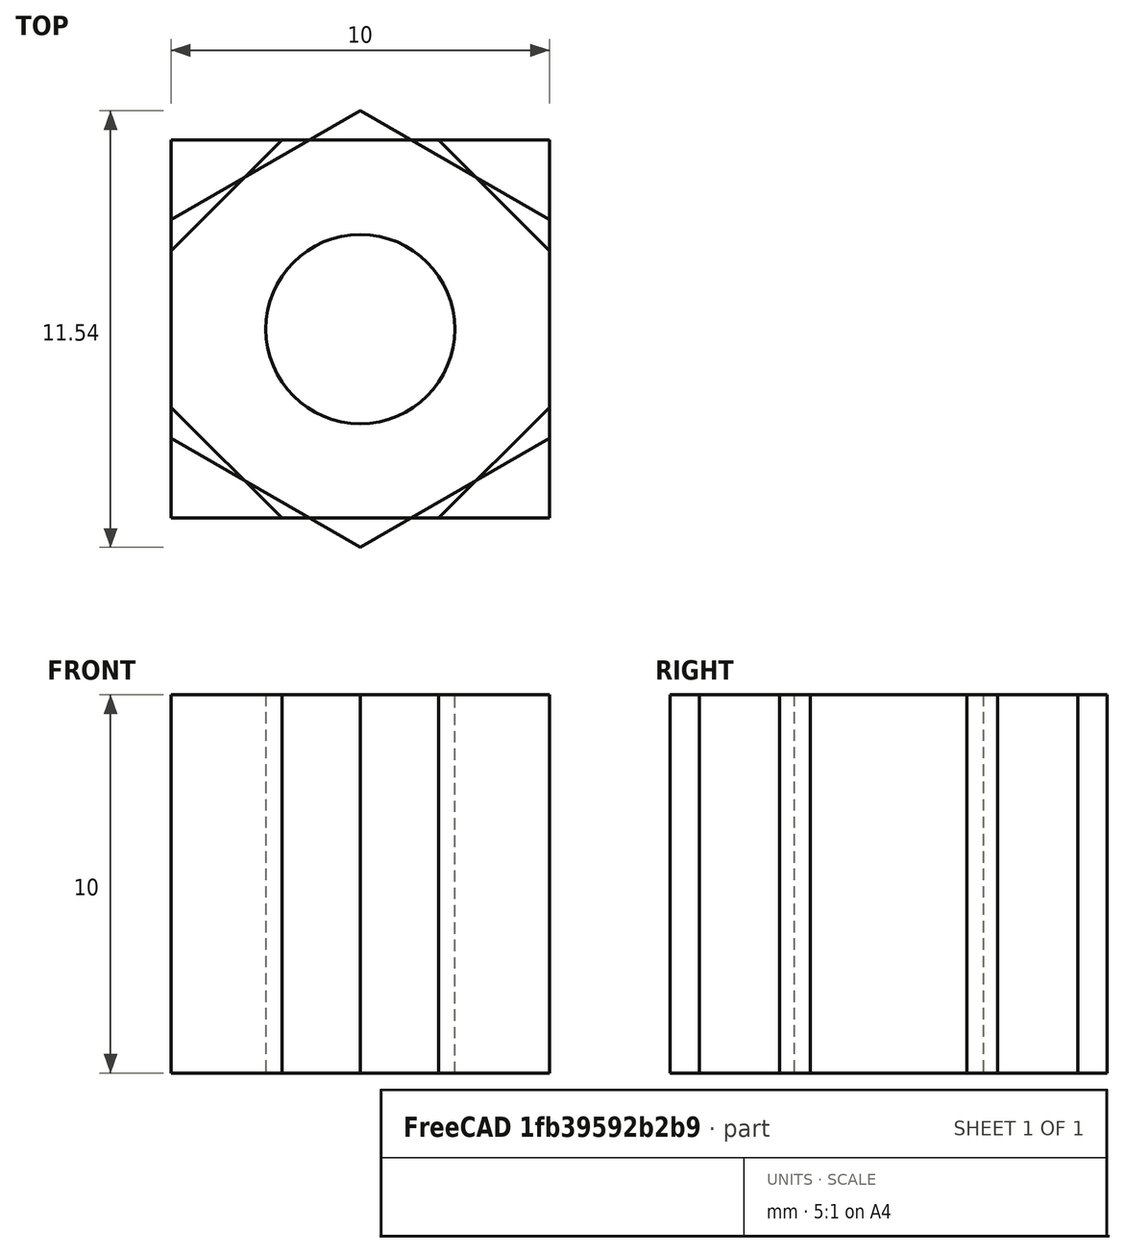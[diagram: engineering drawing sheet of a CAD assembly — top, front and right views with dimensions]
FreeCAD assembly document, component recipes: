
FREECAD ASSEMBLY — COMPONENT RECIPES ("xchg-components-b")

This assembly document has 6 components, labeled P0..P5 below (a component is one placed body or linked part). 6 of them carry a construction recipe — the FreeCAD feature program that regenerates the part from scratch, quoted from this document or its linked companion documents; the rest are supplied as boundary geometry only. No exploded tour is included for this assembly.
COMPONENT P0 — recipe-attached ("Cylinder 001", modeled in this document).
Construction recipe (the document's own serialized feature program — sketch geometry with constraints, then the solid features built on it; lengths are millimeters unless a unit is written):

FEATURE [Sketcher::SketchObject] Sketch
  MapMode = 5
  Support = -> [XY_Plane]
  sketch-geometry (1):
    g0: Circle CenterX=0 CenterY=0 CenterZ=0 NormalX=0 NormalY=0 NormalZ=1 AngleXU=0 Radius=2.5
  constraints (2):
    c: Coincident(g0,g-1)
    c: Diameter(g0) = 5
FEATURE [PartDesign::Pad] Pad
  ClaimChildren = false
  Length = 10
  Length2 = 100
  Profile = -> Sketch
  Type = 0
FEATURE [PartDesign::Body] Body  label="Cylinder 000"
  Group = -> [Sketch,Pad]
  Origin = -> Origin
  Tip = -> Pad
COMPONENT P1 — recipe-attached ("Cube 001", modeled in this document).
Construction recipe (the document's own serialized feature program — sketch geometry with constraints, then the solid features built on it; lengths are millimeters unless a unit is written):

FEATURE [Sketcher::SketchObject] Sketch001
  MapMode = 5
  Support = -> [XY_Plane001]
  sketch-geometry (5):
    g0: LineSegment StartX=5 StartY=5 StartZ=0 EndX=-5 EndY=5 EndZ=0
    g1: LineSegment StartX=-5 StartY=5 StartZ=0 EndX=-5 EndY=-5 EndZ=0
    g2: LineSegment StartX=-5 StartY=-5 StartZ=0 EndX=5 EndY=-5 EndZ=0
    g3: LineSegment StartX=5 StartY=-5 StartZ=0 EndX=5 EndY=5 EndZ=0
    g4: Circle [constr] CenterX=0 CenterY=0 CenterZ=0 NormalX=0 NormalY=0 NormalZ=1 AngleXU=0 Radius=7.07107
  constraints (14):
    c: Coincident(g0,g1)
    c: Coincident(g1,g2)
    c: Coincident(g2,g3)
    c: Coincident(g3,g0)
    c: Equal(g0,g1)
    c: Equal(g0,g2)
    c: Equal(g0,g3)
    c: PointOnObject(g0,g4)
    c: PointOnObject(g1,g4)
    c: PointOnObject(g2,g4)
    c: PointOnObject(g3,g4)
    c: Coincident(g4,g-1)
    c: Horizontal(g0)
    c: Distance(g2) = 10
FEATURE [PartDesign::Pad] Pad001
  ClaimChildren = false
  Length = 10
  Length2 = 100
  Profile = -> Sketch001
  Type = 0
FEATURE [PartDesign::Body] Body001  label="Cube 000"
  Group = -> [Sketch001,Pad001]
  Origin = -> Origin001
  Tip = -> Pad001
COMPONENT P2 — same part as P0; its construction recipe is shown at P0.
COMPONENT P3 — recipe-attached ("Hexagon-Prism 001", modeled in this document).
Construction recipe (the document's own serialized feature program — sketch geometry with constraints, then the solid features built on it; lengths are millimeters unless a unit is written):

FEATURE [Sketcher::SketchObject] Sketch002
  MapMode = 5
  Support = -> [XY_Plane002]
  sketch-geometry (7):
    g0: LineSegment StartX=0 StartY=5.7735 StartZ=0 EndX=-5 EndY=2.88675 EndZ=0
    g1: LineSegment StartX=-5 StartY=2.88675 StartZ=0 EndX=-5 EndY=-2.88675 EndZ=0
    g2: LineSegment StartX=-5 StartY=-2.88675 StartZ=0 EndX=-9e-16 EndY=-5.7735 EndZ=0
    g3: LineSegment StartX=-6e-16 StartY=-5.7735 StartZ=0 EndX=5 EndY=-2.88675 EndZ=0
    g4: LineSegment StartX=5 StartY=-2.88675 StartZ=0 EndX=5 EndY=2.88675 EndZ=0
    g5: LineSegment StartX=5 StartY=2.88675 StartZ=0 EndX=0 EndY=5.7735 EndZ=0
    g6: Circle [constr] CenterX=0 CenterY=0 CenterZ=0 NormalX=0 NormalY=0 NormalZ=1 AngleXU=0 Radius=5.7735
  constraints (16):
    c: Coincident(g0,g1)
    c: Coincident(g1,g2)
    c: Coincident(g2,g3)
    c: Coincident(g3,g4)
    c: Coincident(g4,g5)
    c: Coincident(g5,g0)
    c: Equal(g0, g1-g5) x5
    c: PointOnObject(g0,g6)
    c: PointOnObject(g1,g6)
    c: PointOnObject(g2,g6)
    c: PointOnObject(g3,g6)
    c: PointOnObject(g4,g6)
    c: PointOnObject(g5,g6)
    c: PointOnObject(g5,g-2)
    c: Coincident(g6,g-1)
    c: Distance(g1,g3) = 10
FEATURE [PartDesign::Pad] Pad002
  ClaimChildren = false
  Length = 10
  Length2 = 100
  Profile = -> Sketch002
  Type = 0
FEATURE [PartDesign::Body] Body002  label="Hexagon-Prism 000"
  Group = -> [Sketch002,Pad002]
  Origin = -> Origin002
  Tip = -> Pad002
COMPONENT P4 — same part as P0; its construction recipe is shown at P0.
COMPONENT P5 — recipe-attached ("Octagon-Prism 001", modeled in this document).
Construction recipe (the document's own serialized feature program — sketch geometry with constraints, then the solid features built on it; lengths are millimeters unless a unit is written):

FEATURE [Sketcher::SketchObject] Sketch003
  MapMode = 5
  Support = -> [XY_Plane003]
  sketch-geometry (9):
    g0: LineSegment StartX=2.07107 StartY=5 StartZ=0 EndX=-2.07107 EndY=5 EndZ=0
    g1: LineSegment StartX=-2.07107 StartY=5 StartZ=0 EndX=-5 EndY=2.07107 EndZ=0
    g2: LineSegment StartX=-5 StartY=2.07107 StartZ=0 EndX=-5 EndY=-2.07107 EndZ=0
    g3: LineSegment StartX=-5 StartY=-2.07107 StartZ=0 EndX=-2.07107 EndY=-5 EndZ=0
    g4: LineSegment StartX=-2.07107 StartY=-5 StartZ=0 EndX=2.07107 EndY=-5 EndZ=0
    g5: LineSegment StartX=2.07107 StartY=-5 StartZ=0 EndX=5 EndY=-2.07107 EndZ=0
    g6: LineSegment StartX=5 StartY=-2.07107 StartZ=0 EndX=5 EndY=2.07107 EndZ=0
    g7: LineSegment StartX=5 StartY=2.07107 StartZ=0 EndX=2.07107 EndY=5 EndZ=0
    g8: Circle [constr] CenterX=0 CenterY=0 CenterZ=0 NormalX=0 NormalY=0 NormalZ=1 AngleXU=0 Radius=5.41196
  constraints (20):
    c: Coincident(g0,g1)
    c: Coincident(g1,g2)
    c: Coincident(g2,g3)
    c: Coincident(g3,g4)
    c: Coincident(g4,g5)
    c: Coincident(g5,g6)
    c: Coincident(g6,g7)
    c: Coincident(g7,g0)
    c: Equal(g0, g1-g7) x7
    c: PointOnObject(g0,g8)
    c: PointOnObject(g1,g8)
    c: PointOnObject(g2,g8)
    c: PointOnObject(g3,g8)
    c: PointOnObject(g4,g8)
    c: PointOnObject(g5,g8)
    c: PointOnObject(g6,g8)
    c: PointOnObject(g7,g8)
    c: Coincident(g8,g-1)
    c: Horizontal(g0)
    c: Distance(g2,g5) = 10
FEATURE [PartDesign::Pad] Pad003
  ClaimChildren = false
  Length = 10
  Length2 = 100
  Profile = -> Sketch003
  Type = 0
FEATURE [PartDesign::Body] Body003  label="Octagon-Prism 000"
  Group = -> [Sketch003,Pad003]
  Origin = -> Origin003
  Tip = -> Pad003
PROVENANCE & LICENSES
A FreeCAD (.FCStd) document from a public repository crawl; recipes are the document's own serialized feature recipes (and, for linked parts, companion documents' recipes).
License: as declared in the source repository (recorded in the dataset sidecar).
